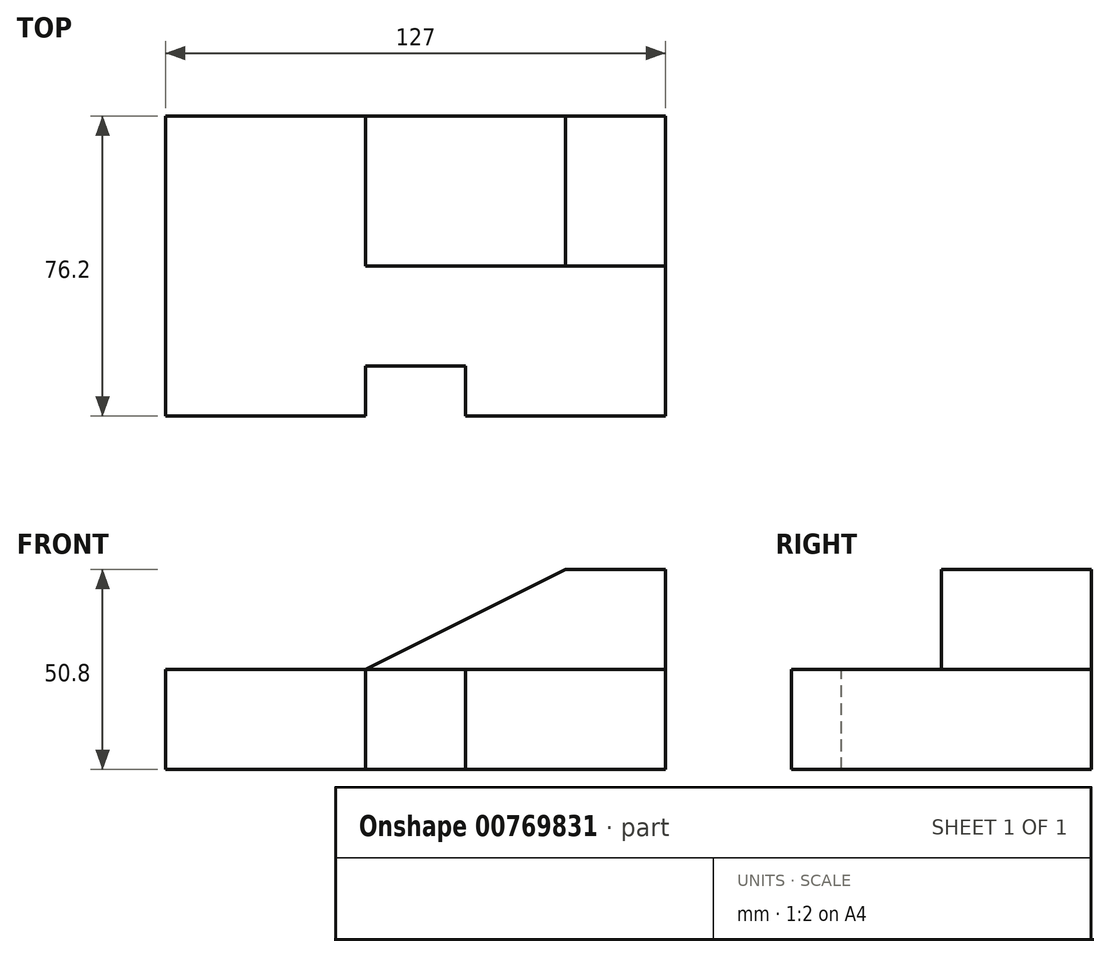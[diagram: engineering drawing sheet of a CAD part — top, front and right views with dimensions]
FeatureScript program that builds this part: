
annotation { "Feature Type Name" : "Feature", "Feature Type Description" : "" }
export const myFeature = defineFeature(function(context is Context, id is Id, definition is map)
    precondition{}
    {
        {
            var Q0;
            Q0=qCreatedBy(makeId("Front.planeOp"),FACE);
            var sketch = newSketch(context, id + "F0", { "sketchPlane" : qUnion([Q0])});
            skLineSegment(sketch, "E0", {"start": v(0, 25.4) * mm, "end": v(127, 25.4) * mm});
            skLineSegment(sketch, "E1", {"start": v(127, 25.4) * mm, "end": v(127, 0) * mm});
            skLineSegment(sketch, "E2", {"start": v(127, 0) * mm, "end": v(0, 0) * mm});
            skLineSegment(sketch, "E3", {"start": v(0, 0) * mm, "end": v(0, 25.4) * mm});
            skSolve(sketch);
        }
        {
            var Q0;
            Q0=makeQuery(id+"F0.imprint","IMPRINT",FACE,{"disambiguationData":[TD([[makeQuery(id+"F0.imprint","IMPRINT",EDGE,{"derivedFrom":sQuery(id+"F0.wireOp",EDGE,"E0")}),-1.0]])]});
            extrude(context, id + "F1", {"entities" : qUnion([Q0]), "endBound" : BoundingType.SYMMETRIC, "depth" : 76.2 * mm, "offsetDistance" : 25.4 * mm});
        }
        {
            var Q0;
            Q0=makeQuery(id+"F1.opExtrude","CAP_FACE",FACE,{"disambiguationData":[OSD([sQuery(id+"F0.wireOp",EDGE,"E0"),sQuery(id+"F0.wireOp",EDGE,"E1"),sQuery(id+"F0.wireOp",EDGE,"E2"),sQuery(id+"F0.wireOp",EDGE,"E3")])],"isStart":true});
            var sketch = newSketch(context, id + "F2", { "sketchPlane" : qUnion([Q0])});
            skLineSegment(sketch, "E4", {"start": v(-127, 25.4) * mm, "end": v(-127, 50.8) * mm});
            skLineSegment(sketch, "E5", {"start": v(-127, 50.8) * mm, "end": v(-101.6, 50.8) * mm});
            skLineSegment(sketch, "E6", {"start": v(-101.6, 50.8) * mm, "end": v(-50.8, 25.4) * mm});
            skLineSegment(sketch, "E7", {"start": v(-50.8, 25.4) * mm, "end": v(-127, 25.4) * mm});
            skSolve(sketch);
        }
        {
            var Q0;
            Q0=makeQuery(id+"F2.imprint","IMPRINT",FACE,{"disambiguationData":[TD([[makeQuery(id+"F2.imprint","IMPRINT",EDGE,{"derivedFrom":sQuery(id+"F2.wireOp",EDGE,"E4")}),-1.0]])]});
            extrude(context, id + "F3", {"entities" : qUnion([Q0]), "oppositeDirection" : true, "depth" : 38.1 * mm, "offsetDistance" : 25.4 * mm});
        }
        {
            var Q0;
            Q0=makeQuery(id+"F1.opExtrude","SWEPT_FACE",FACE,{"disambiguationData":[OSD([sQuery(id+"F0.wireOp",EDGE,"E0")])]});
            var sketch = newSketch(context, id + "F4", { "sketchPlane" : qUnion([Q0])});
            skLineSegment(sketch, "E8.bottom", {"start": v(50.8, -38.1) * mm, "end": v(76.2, -38.1) * mm});
            skLineSegment(sketch, "E8.top", {"start": v(50.8, -25.4) * mm, "end": v(76.2, -25.4) * mm});
            skLineSegment(sketch, "E8.left", {"start": v(50.8, -38.1) * mm, "end": v(50.8, -25.4) * mm});
            skLineSegment(sketch, "E8.right", {"start": v(76.2, -38.1) * mm, "end": v(76.2, -25.4) * mm});
            skSolve(sketch);
        }
        {
            var Q0;
            Q0=makeQuery(id+"F4.imprint","IMPRINT",FACE,{"disambiguationData":[TD([[makeQuery(id+"F4.imprint","IMPRINT",EDGE,{"derivedFrom":sQuery(id+"F4.wireOp",EDGE,"E8.bottom")}),1.0]])]});
            extrude(context, id + "F5", {"entities" : qUnion([Q0]), "operationType" : NewBodyOperationType.REMOVE, "endBound" : BoundingType.THROUGH_ALL, "oppositeDirection" : true, "depth" : 25.4 * mm, "offsetDistance" : 25.4 * mm});
        }
    });
